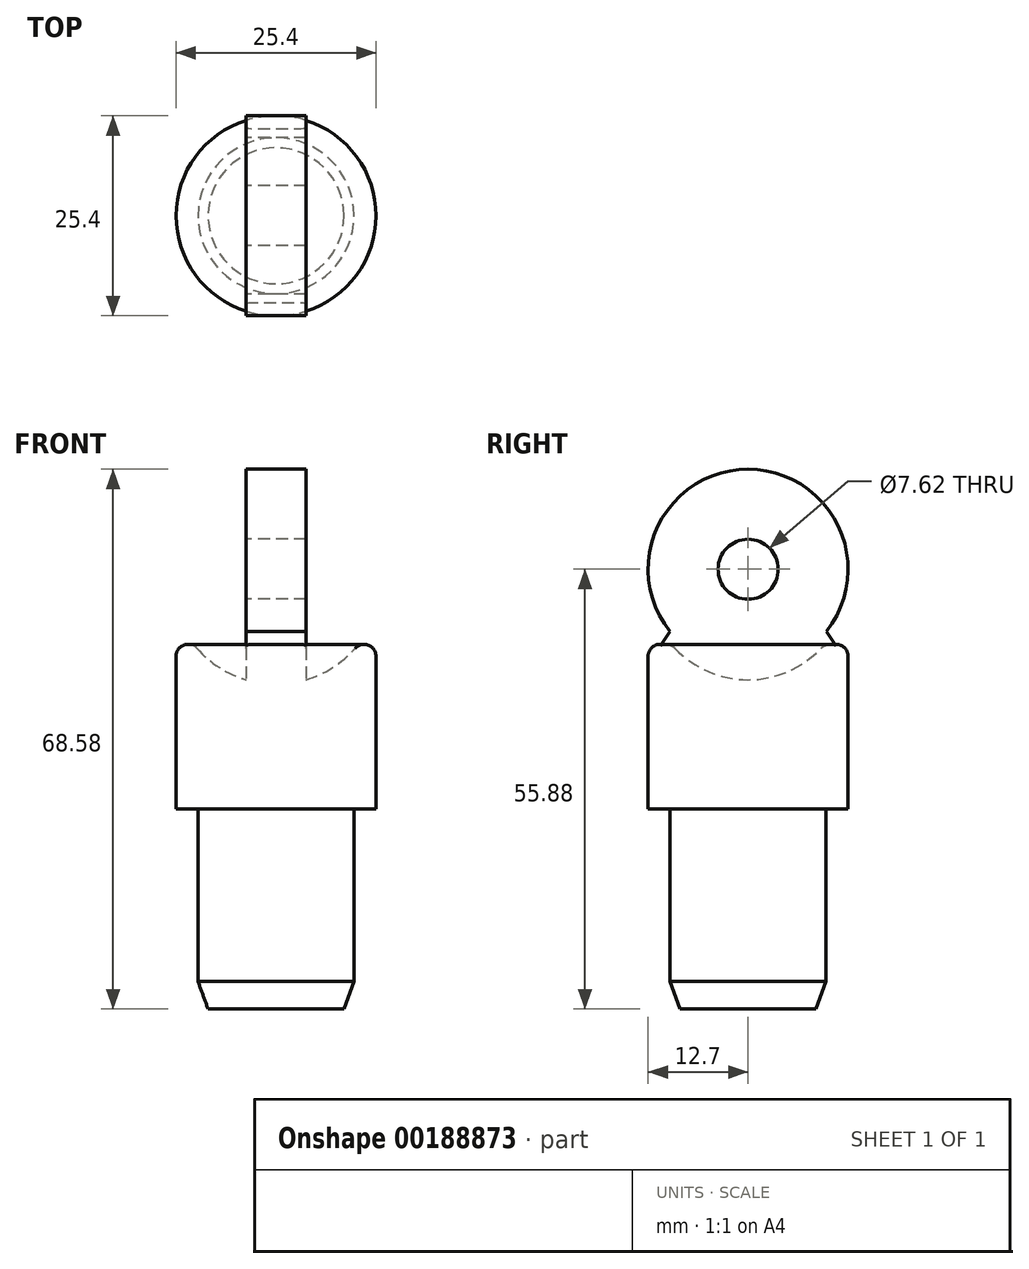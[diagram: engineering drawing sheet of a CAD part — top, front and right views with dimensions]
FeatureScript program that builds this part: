
annotation { "Feature Type Name" : "Feature", "Feature Type Description" : "" }
export const myFeature = defineFeature(function(context is Context, id is Id, definition is map)
    precondition{}
    {
        {
            var Q0;
            Q0=qCreatedBy(makeId("Top.planeOp"),FACE);
            var sketch = newSketch(context, id + "F0", { "sketchPlane" : qUnion([Q0])});
            skCircle(sketch, "E0", {"center": v(0, 0) * mm, "radius": 12.7 * mm});
            skSolve(sketch);
        }
        {
            var Q0;
            Q0 = qSketchRegion(id + "F0", true);
            extrude(context, id + "F1", {"entities" : qUnion([Q0]), "depth" : 25.4 * mm});
        }
        {
            var Q0;
            Q0=qCreatedBy(makeId("Right.planeOp"),FACE);
            var sketch = newSketch(context, id + "F2", { "sketchPlane" : qUnion([Q0])});
            skLineSegment(sketch, "E1", {"start": v(0, 0) * mm, "end": v(0, 50.4) * mm, "construction": true});
            skArc(sketch, "E2", {"start": v(0, 42.55) * mm, "mid": v(-13.34, 29.21) * mm, "end": v(0, 15.87) * mm});
            skLineSegment(sketch, "E3", {"start": v(0, 42.55) * mm, "end": v(0, 15.88) * mm});
            skSolve(sketch);
        }
        {
            var Q0;
            Q0 = qSketchRegion(id + "F2", true);
            var Q1;
            Q1=sQuery(id+"F2.wireOp",EDGE,"E1");
            revolve(context, id + "F3", {"operationType" : NewBodyOperationType.REMOVE, "entities" : qUnion([Q0]), "axis" : qUnion([Q1]), "revolveType" : RevolveType.FULL, "oppositeDirection" : true});
        }
        {
            var Q0;
            Q0=qCreatedBy(makeId("Right.planeOp"),FACE);
            var sketch = newSketch(context, id + "F4", { "sketchPlane" : qUnion([Q0])});
            skCircle(sketch, "E4", {"center": v(0, 30.48) * mm, "radius": 12.7 * mm});
            skLineSegment(sketch, "E5", {"start": v(-9.92, 22.56) * mm, "end": v(-12.03, 19.44) * mm});
            skArc(sketch, "E6", {"start": v(-12.03, 19.44) * mm, "mid": v(-6.8, 14.98) * mm, "end": v(0, 13.9) * mm});
            skLineSegment(sketch, "E7", {"start": v(0, 55.74) * mm, "end": v(0, 0) * mm, "construction": true});
            skLineSegment(sketch, "E8.MirrorCS", {"start": v(9.92, 22.56) * mm, "end": v(12.03, 19.44) * mm});
            skArc(sketch, "E9.MirrorCS", {"start": v(12.03, 19.44) * mm, "mid": v(6.8, 14.98) * mm, "end": v(0, 13.9) * mm});
            skCircle(sketch, "E10", {"center": v(0, 30.48) * mm, "radius": 3.81 * mm});
            skSolve(sketch);
        }
        {
            var Q0;
            Q0 = qSketchRegion(id + "F4", true);
            extrude(context, id + "F5", {"entities" : qUnion([Q0]), "operationType" : NewBodyOperationType.ADD, "endBound" : BoundingType.SYMMETRIC, "depth" : 7.62 * mm});
        }
        {
            var Q0;
            Q0=makeQuery(id+"F3.boolean.opBoolean","INTERSECT",EDGE,{"derivedFrom":[makeQuery(id+"F1.opExtrude","SWEPT_FACE",FACE,{"disambiguationData":[OSD([sQuery(id+"F0.wireOp",EDGE,"E0")])]}),makeQuery(id+"F3.opRevolve","SWEPT_FACE",FACE,{"disambiguationData":[OSD([sQuery(id+"F2.wireOp",EDGE,"E2")])]})]});
            fillet(context, id + "F6", {"entities" : qUnion([Q0]), "radius" : 1.52 * mm, "tangentPropagation" : true, "allowEdgeOverflow" : false});
        }
        {
            var Q0;
            Q0=makeQuery(id+"F1.opExtrude","CAP_FACE",FACE,{"disambiguationData":[OSD([sQuery(id+"F0.wireOp",EDGE,"E0")])],"isStart":true});
            var sketch = newSketch(context, id + "F7", { "sketchPlane" : qUnion([Q0])});
            skCircle(sketch, "E11", {"center": v(0, 0) * mm, "radius": 9.9 * mm});
            skSolve(sketch);
        }
        {
            var Q0;
            Q0 = qSketchRegion(id + "F7", true);
            extrude(context, id + "F8", {"entities" : qUnion([Q0]), "operationType" : NewBodyOperationType.ADD, "depth" : 25.4 * mm});
        }
        {
            var Q0;
            Q0=makeQuery(id+"F8.opExtrude","CAP_EDGE",EDGE,{"disambiguationData":[OSD([sQuery(id+"F7.wireOp",EDGE,"E11")])],"isStart":false});
            chamfer(context, id + "F9", {"entities" : qUnion([Q0]), "chamferType" : ChamferType.OFFSET_ANGLE, "width" : 1.27 * mm, "oppositeDirection" : false, "angle" : 70 * degree, "tangentPropagation" : true});
        }
    });
